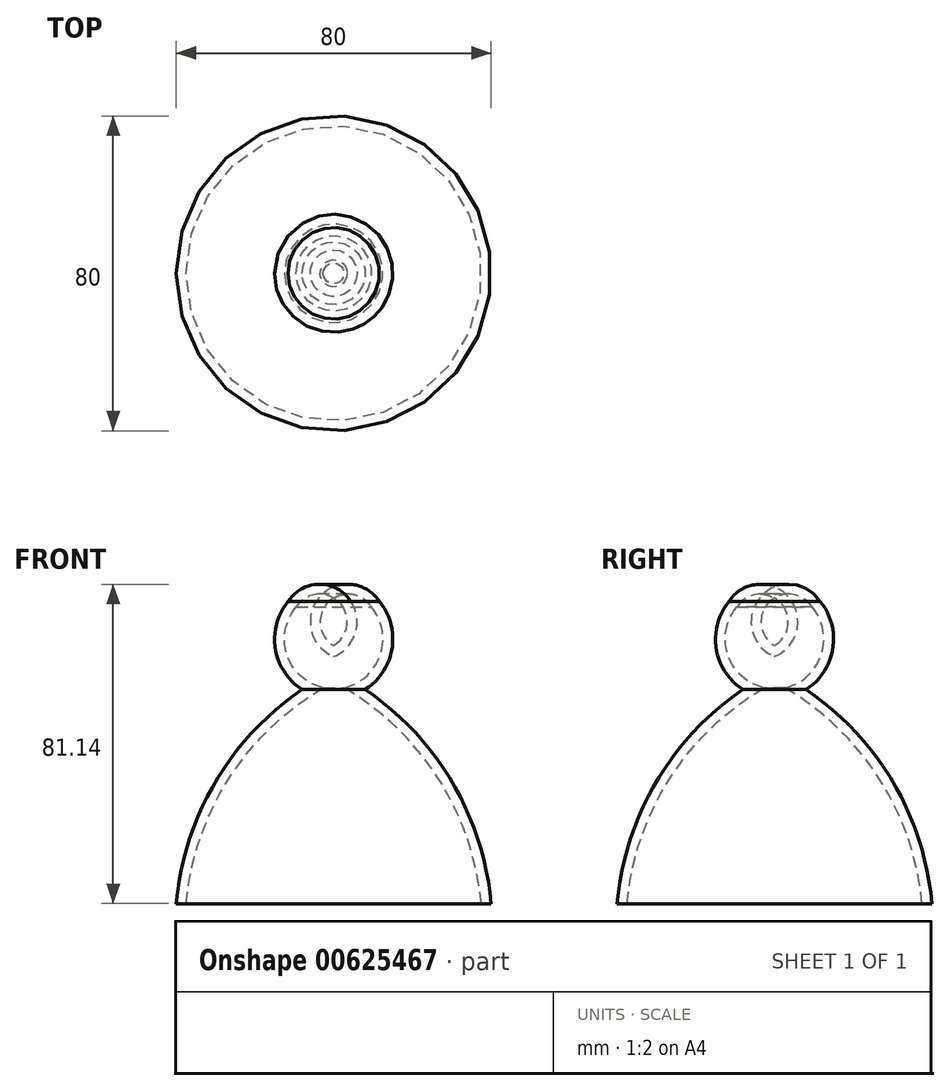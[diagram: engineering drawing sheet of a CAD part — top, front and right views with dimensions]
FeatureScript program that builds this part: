
annotation { "Feature Type Name" : "Feature", "Feature Type Description" : "" }
export const myFeature = defineFeature(function(context is Context, id is Id, definition is map)
    precondition{}
    {
        {
            var Q0;
            Q0=qCreatedBy(makeId("Front.planeOp"),FACE);
            var sketch = newSketch(context, id + "F0", { "sketchPlane" : qUnion([Q0])});
            skArc(sketch, "E0", {"start": v(-17.17, 20.49) * mm, "mid": v(-39.29, -3.11) * mm, "end": v(-49.17, -33.91) * mm});
            skArc(sketch, "E1", {"start": v(-20.77, 42.89) * mm, "mid": v(-23.99, 30.88) * mm, "end": v(-17.17, 20.49) * mm});
            skArc(sketch, "E2", {"start": v(-9.17, 46.52) * mm, "mid": v(-15.62, 46.8) * mm, "end": v(-20.77, 42.89) * mm});
            skLineSegment(sketch, "E3", {"start": v(-49.17, -33.91) * mm, "end": v(-9.17, -33.91) * mm});
            skLineSegment(sketch, "E4", {"start": v(-9.17, -33.91) * mm, "end": v(-9.17, 46.52) * mm});
            skSolve(sketch);
        }
        {
            var Q0;
            Q0=makeQuery(id+"F0.imprint","IMPRINT",FACE,{"disambiguationData":[TD([[makeQuery(id+"F0.imprint","IMPRINT",EDGE,{"derivedFrom":sQuery(id+"F0.wireOp",EDGE,"E0")}),1.0]])]});
            var Q1;
            Q1=sQuery(id+"F0.wireOp",EDGE,"E4");
            revolve(context, id + "F1", {"entities" : qUnion([Q0]), "axis" : qUnion([Q1]), "revolveType" : RevolveType.FULL});
        }
        {
            var Q0;
            Q0=makeQuery(id+"F1.opRevolve","SWEPT_FACE",FACE,{"disambiguationData":[OSD([sQuery(id+"F0.wireOp",EDGE,"E3")])]});
            shell(context, id + "F2", {"entities" : qUnion([Q0]), "thickness" : 2.5 * mm});
        }
    });
